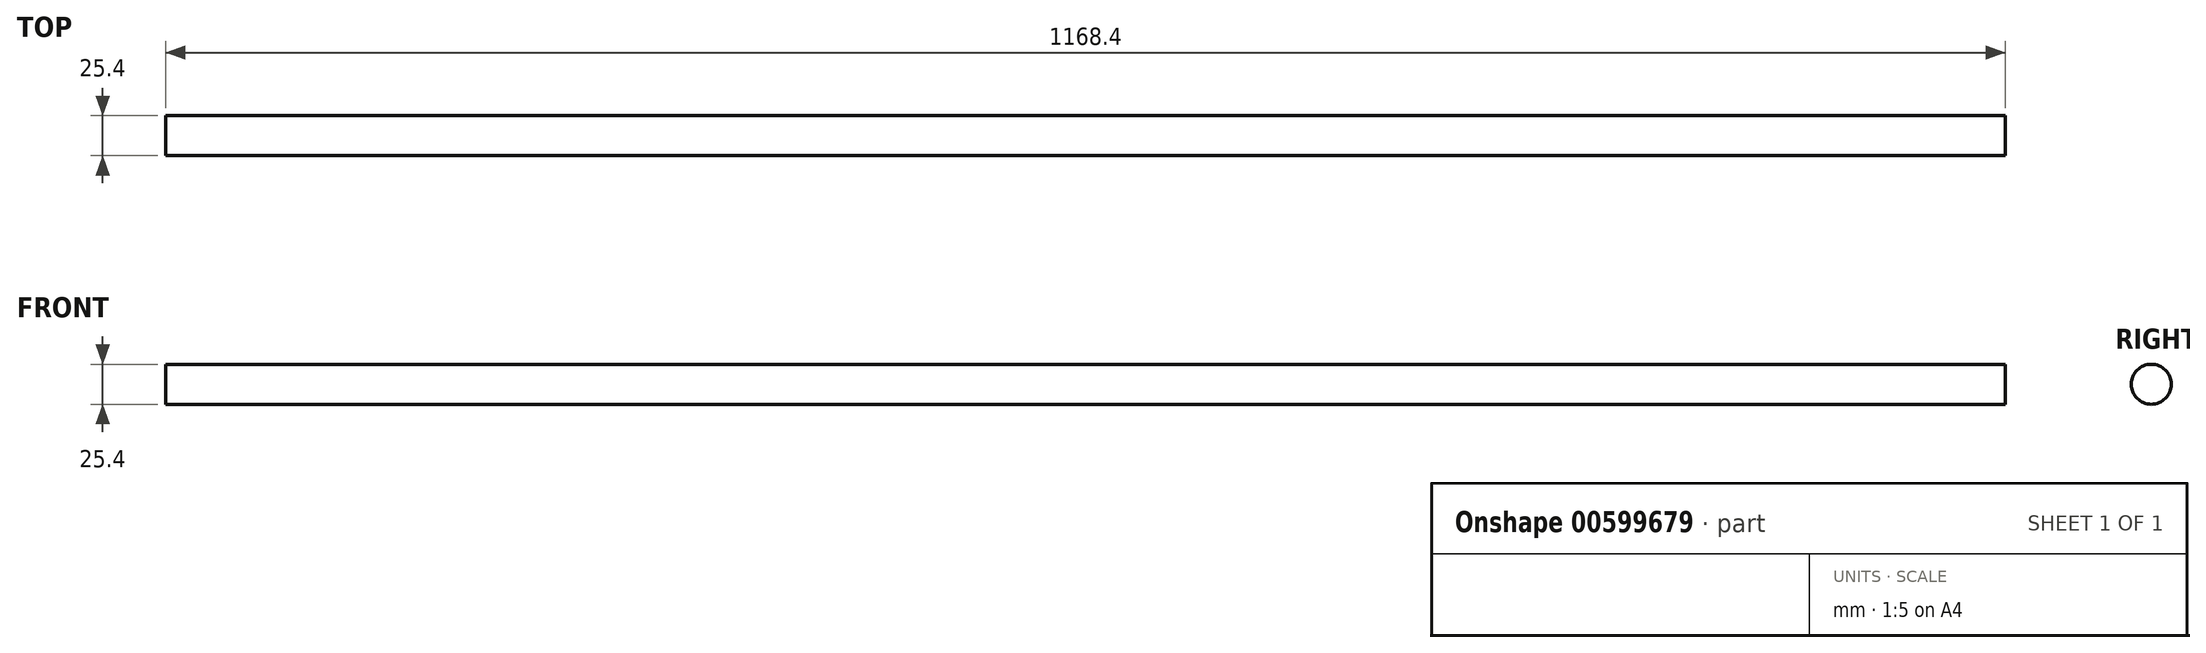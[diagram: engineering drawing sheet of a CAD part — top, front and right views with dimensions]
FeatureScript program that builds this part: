
annotation { "Feature Type Name" : "Feature", "Feature Type Description" : "" }
export const myFeature = defineFeature(function(context is Context, id is Id, definition is map)
    precondition{}
    {
        {
            var Q0;
            Q0=qCreatedBy(makeId("Right.planeOp"),FACE);
            var sketch = newSketch(context, id + "F0", { "sketchPlane" : qUnion([Q0])});
            skCircle(sketch, "E0", {"center": v(0, 0) * mm, "radius": 12.7 * mm});
            skSolve(sketch);
        }
        {
            var Q0;
            Q0=makeQuery(id+"F0.imprint","IMPRINT",FACE,{"disambiguationData":[TD([[makeQuery(id+"F0.imprint","IMPRINT",EDGE,{"derivedFrom":sQuery(id+"F0.wireOp",EDGE,"E0")}),1.0]])]});
            extrude(context, id + "F1", {"entities" : qUnion([Q0]), "depth" : 1168.4 * mm, "offsetDistance" : 25.4 * mm});
        }
    });
